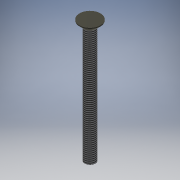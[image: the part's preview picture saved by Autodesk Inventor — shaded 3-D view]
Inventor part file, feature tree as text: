
AUTODESK INVENTOR PART (.ipt)
format: ipt  version: 2016 (Build 200138000, 138)  size: 129,536 bytes
history: native  units: mm
features: extrude x5, sketch x5, other x1, thread x1, chamfer x1
ambient origin geometry x1: Origin
bodies: Body1 (feature_tree)
feature tree (13):
  other  "ソリッド1"
  extrude  "押し出し1"  Depth=3.0mm
  extrude  "押し出し2"  Depth=6.0mm TaperAngle=0.0deg
  thread  "ねじ1"
  chamfer  "面取り1"  Distance=6.0mm
  extrude  "押し出し4"  Depth=1.75mm TaperAngle=0.0deg
  extrude  "押し出し5"  Depth=10.0mm TaperAngle=0.0deg
  extrude  "押し出し6"  Depth=1.5mm TaperAngle=45.0deg
  sketch  "スケッチ1"
  sketch  "スケッチ2"
  sketch  "スケッチ4"
  sketch  "スケッチ5"
  sketch  "スケッチ6"
